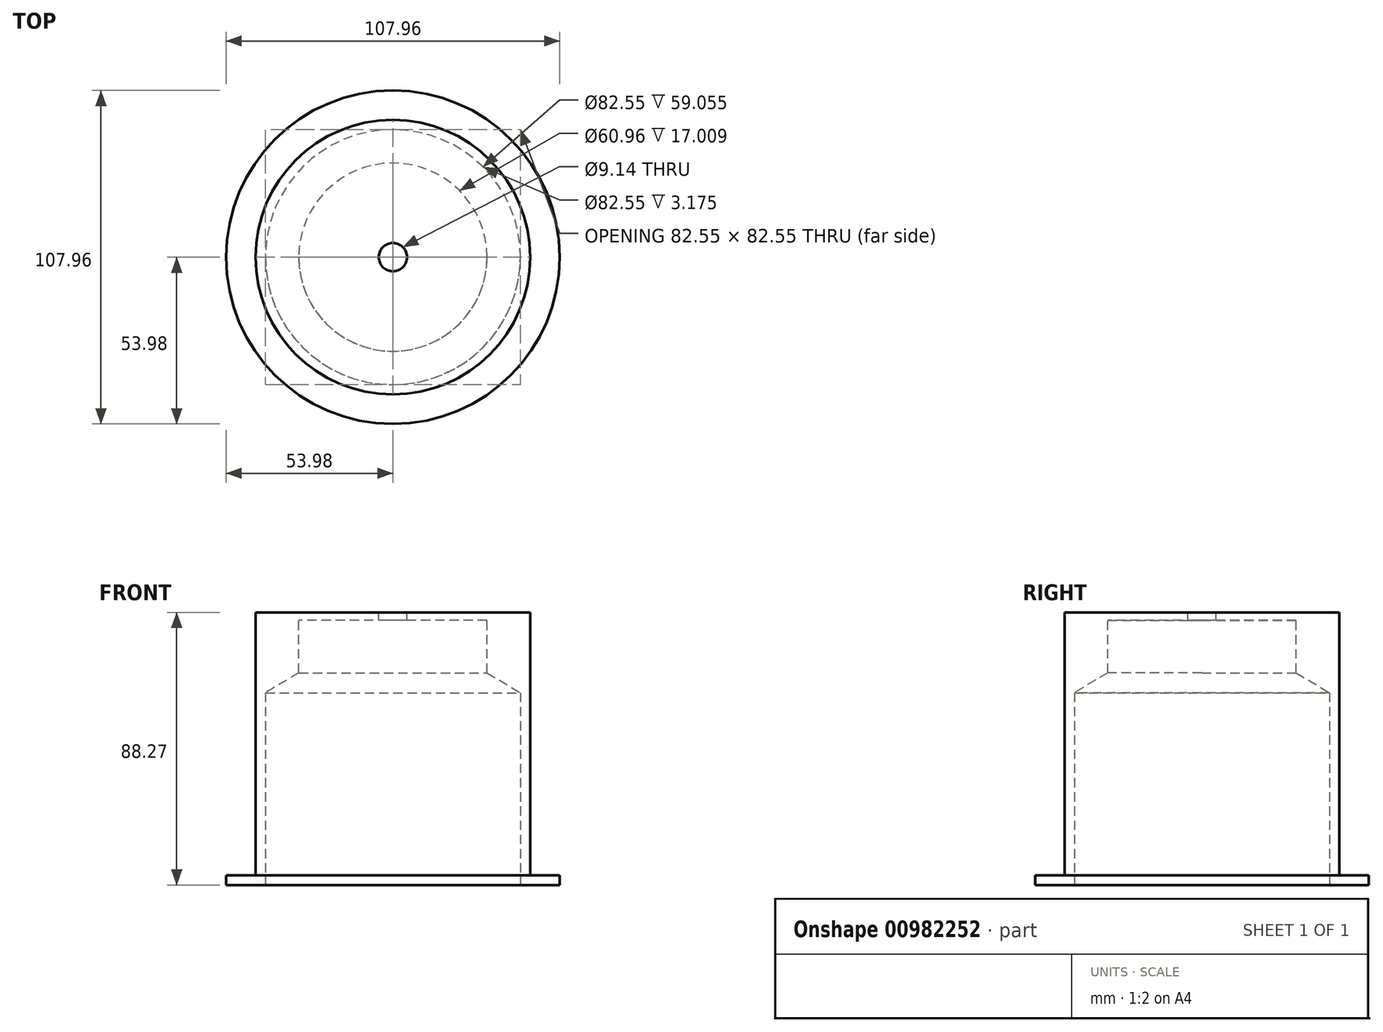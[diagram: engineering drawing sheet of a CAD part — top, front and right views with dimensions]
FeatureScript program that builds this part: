
annotation { "Feature Type Name" : "Feature", "Feature Type Description" : "" }
export const myFeature = defineFeature(function(context is Context, id is Id, definition is map)
    precondition{}
    {
        {
            var Q0;
            Q0=qCreatedBy(makeId("Top.planeOp"),FACE);
            var sketch = newSketch(context, id + "F0", { "sketchPlane" : qUnion([Q0])});
            skCircle(sketch, "E0", {"center": v(0, 0) * mm, "radius": 53.98 * mm});
            skSolve(sketch);
        }
        {
            var Q0;
            Q0=makeQuery(id+"F0.imprint","IMPRINT",FACE,{"disambiguationData":[TD([[makeQuery(id+"F0.imprint","IMPRINT",EDGE,{"derivedFrom":sQuery(id+"F0.wireOp",EDGE,"E0")}),1.0]])]});
            extrude(context, id + "F1", {"entities" : qUnion([Q0]), "depth" : 3.17 * mm, "offsetDistance" : 25.4 * mm});
        }
        {
            var Q0;
            Q0=makeQuery(id+"F1.opExtrude","CAP_FACE",FACE,{"disambiguationData":[OSD([sQuery(id+"F0.wireOp",EDGE,"E0")])],"isStart":false});
            var sketch = newSketch(context, id + "F2", { "sketchPlane" : qUnion([Q0])});
            skCircle(sketch, "E1", {"center": v(0, 0) * mm, "radius": 44.45 * mm});
            skSolve(sketch);
        }
        {
            var Q0;
            Q0=makeQuery(id+"F2.imprint","IMPRINT",FACE,{"disambiguationData":[TD([[makeQuery(id+"F2.imprint","IMPRINT",EDGE,{"derivedFrom":sQuery(id+"F2.wireOp",EDGE,"E1")}),1.0]])]});
            var Q1;
            Q1=sQuery(id+"F2.wireOp",EDGE,"E1");
            extrude(context, id + "F3", {"entities" : qUnion([Q0]), "surfaceEntities" : qUnion([Q1]), "depth" : 63.5 * mm, "offsetDistance" : 25.4 * mm});
        }
        {
            var Q0;
            Q0=makeQuery(id+"F3.opExtrude","CAP_FACE",FACE,{"disambiguationData":[OSD([sQuery(id+"F2.wireOp",EDGE,"E1")])],"isStart":false});
            var sketch = newSketch(context, id + "F4", { "sketchPlane" : qUnion([Q0])});
            skCircle(sketch, "E2", {"center": v(0, 0) * mm, "radius": 44.45 * mm});
            skSolve(sketch);
        }
        {
            var Q0;
            Q0=makeQuery(id+"F4.imprint","IMPRINT",FACE,{"disambiguationData":[TD([[makeQuery(id+"F4.imprint","IMPRINT",EDGE,{"derivedFrom":sQuery(id+"F4.wireOp",EDGE,"E2")}),1.0]])]});
            extrude(context, id + "F5", {"entities" : qUnion([Q0]), "operationType" : NewBodyOperationType.ADD, "depth" : 19.05 * mm, "offsetDistance" : 25.4 * mm});
        }
        {
            var Q0;
            Q0=makeQuery(id+"F1.opExtrude","CAP_FACE",FACE,{"disambiguationData":[OSD([sQuery(id+"F0.wireOp",EDGE,"E0")])],"isStart":true});
            var sketch = newSketch(context, id + "F6", { "sketchPlane" : qUnion([Q0])});
            skPoint(sketch, "E3", {"position": v(0, 0) * mm});
            skSolve(sketch);
        }
        {
            var Q0;
            Q0=sQuery(id+"F6.wireOp",VERTEX,"E3");
            var Q1;
            Q1=makeQuery(id+"F3.opExtrude","SWEPT_BODY",BODY,{"disambiguationData":[OSD([sQuery(id+"F2.wireOp",EDGE,"E1")])]});
            var Q2;
            Q2=makeQuery(id+"F1.opExtrude","SWEPT_BODY",BODY,{"disambiguationData":[OSD([sQuery(id+"F0.wireOp",EDGE,"E0")])]});
            hole(context, id + "F7", {"style" : HoleStyle.SIMPLE, "endStyle" : HoleEndStyle.BLIND, "holeDiameter" : 82.55 * mm, "majorDiameter" : 6.35 * mm, "holeDepth" : 62.23 * mm, "isTappedThrough" : true, "tappedDepth" : 12.7 * mm, "tapClearance" : 3, "locations" : qUnion([Q0]), "scope" : qUnion([Q1, Q2])});
        }
        {
            var Q0;
            Q0=makeQuery(id+"F5.opExtrude","CAP_FACE",FACE,{"disambiguationData":[OSD([sQuery(id+"F4.wireOp",EDGE,"E2")])],"isStart":false});
            var sketch = newSketch(context, id + "F8", { "sketchPlane" : qUnion([Q0])});
            skPoint(sketch, "E4", {"position": v(0, 0) * mm});
            skSolve(sketch);
        }
        {
            var Q0;
            Q0=sQuery(id+"F8.wireOp",VERTEX,"E4");
            var Q1;
            Q1=makeQuery(id+"F3.opExtrude","SWEPT_BODY",BODY,{"disambiguationData":[OSD([sQuery(id+"F2.wireOp",EDGE,"E1")])]});
            hole(context, id + "F9", {"style" : HoleStyle.SIMPLE, "endStyle" : HoleEndStyle.BLIND, "holeDiameter" : 60.96 * mm, "majorDiameter" : 6.35 * mm, "holeDepth" : 17.78 * mm, "isTappedThrough" : true, "tappedDepth" : 12.7 * mm, "tapClearance" : 3, "locations" : qUnion([Q0]), "scope" : qUnion([Q1])});
        }
        {
            var Q0;
            Q0=makeQuery(id+"F5.opExtrude","CAP_FACE",FACE,{"disambiguationData":[OSD([sQuery(id+"F4.wireOp",EDGE,"E2")])],"isStart":false});
            var sketch = newSketch(context, id + "F10", { "sketchPlane" : qUnion([Q0])});
            skCircle(sketch, "E5", {"center": v(0, 0) * mm, "radius": 44.45 * mm});
            skSolve(sketch);
        }
        {
            var Q0;
            Q0 = qSketchRegion(id + "F10", true);
            extrude(context, id + "F11", {"entities" : qUnion([Q0]), "operationType" : NewBodyOperationType.ADD, "depth" : 2.54 * mm, "offsetDistance" : 25.4 * mm});
        }
        {
            var Q0;
            Q0=makeQuery(id+"F11.opExtrude","CAP_FACE",FACE,{"disambiguationData":[OSD([sQuery(id+"F10.wireOp",EDGE,"E5")])],"isStart":false});
            var sketch = newSketch(context, id + "F12", { "sketchPlane" : qUnion([Q0])});
            skPoint(sketch, "E6", {"position": v(0, 0) * mm});
            skSolve(sketch);
        }
        {
            var Q0;
            Q0=sQuery(id+"F12.wireOp",VERTEX,"E6");
            var Q1;
            Q1=makeQuery(id+"F3.opExtrude","SWEPT_BODY",BODY,{"disambiguationData":[OSD([sQuery(id+"F2.wireOp",EDGE,"E1")])]});
            hole(context, id + "F13", {"style" : HoleStyle.SIMPLE, "endStyle" : HoleEndStyle.BLIND, "holeDiameter" : 9.14 * mm, "majorDiameter" : 6.35 * mm, "holeDepth" : 17.78 * mm, "isTappedThrough" : true, "tappedDepth" : 12.7 * mm, "tapClearance" : 3, "locations" : qUnion([Q0]), "scope" : qUnion([Q1])});
        }
    });
